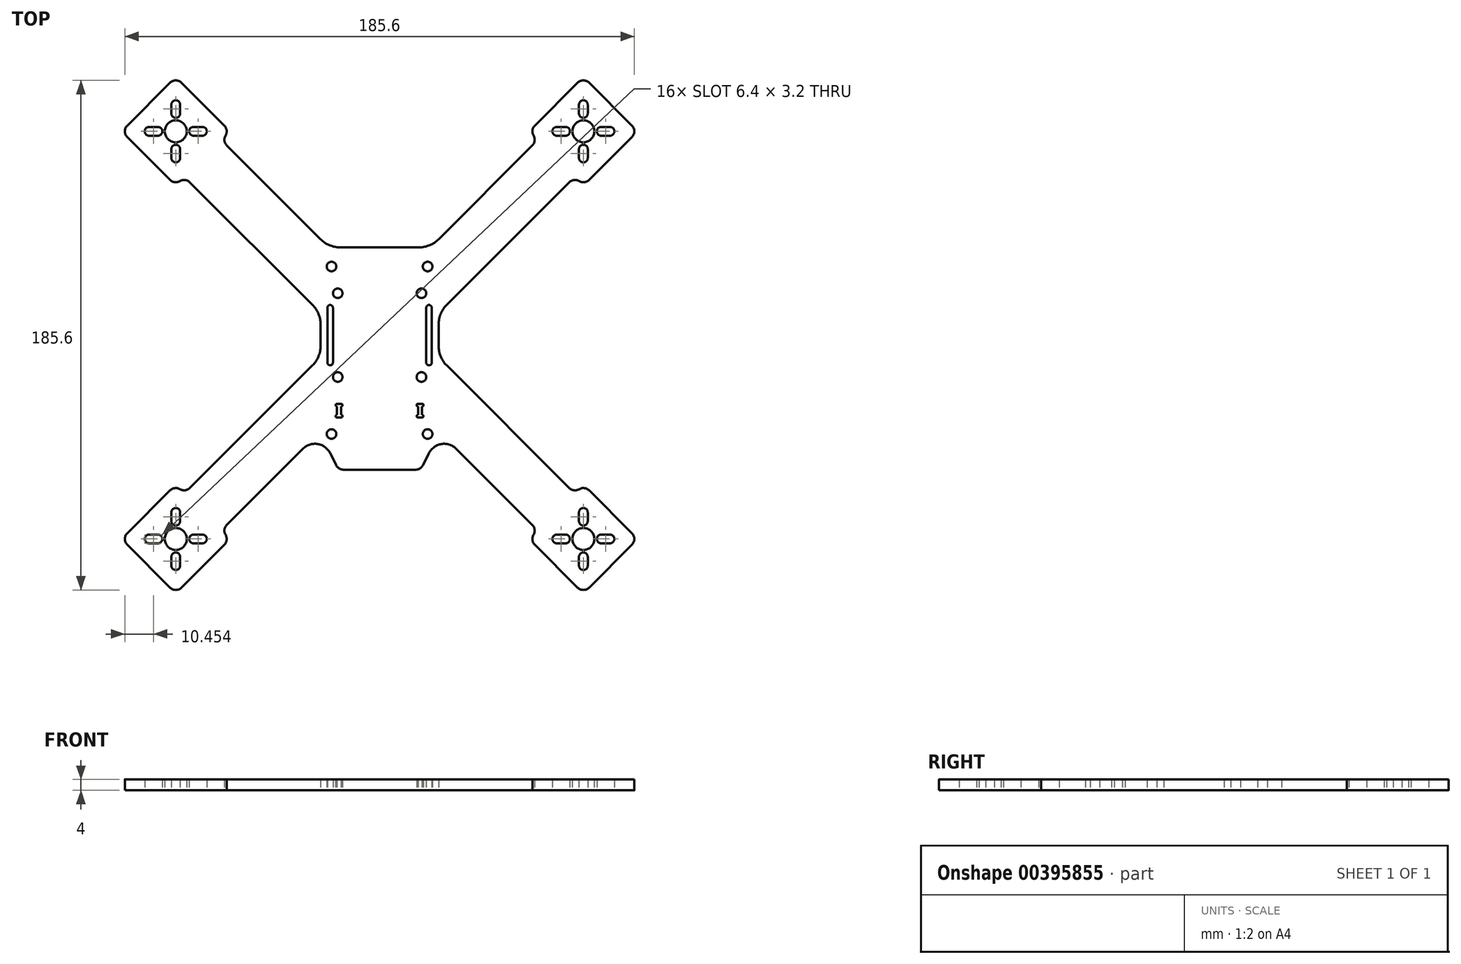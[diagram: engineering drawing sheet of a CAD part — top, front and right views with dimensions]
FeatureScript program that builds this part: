
annotation { "Feature Type Name" : "Feature", "Feature Type Description" : "" }
export const myFeature = defineFeature(function(context is Context, id is Id, definition is map)
    precondition{}
    {
        {
            var Q0;
            Q0=qCreatedBy(makeId("Top.planeOp"),FACE);
            var sketch = newSketch(context, id + "F0", { "sketchPlane" : qUnion([Q0])});
            skLineSegment(sketch, "E0.left", {"start": v(-21.5, 3.92) * mm, "end": v(-21.5, -3.92) * mm});
            skCircle(sketch, "E1", {"center": v(-15.25, 15.25) * mm, "radius": 1.75 * mm});
            skCircle(sketch, "E2", {"center": v(-15.25, -15.25) * mm, "radius": 1.75 * mm});
            skCircle(sketch, "E3.MirrorC", {"center": v(15.25, 15.25) * mm, "radius": 1.75 * mm});
            skCircle(sketch, "E4.MirrorC", {"center": v(15.25, -15.25) * mm, "radius": 1.75 * mm});
            skCircle(sketch, "E5", {"center": v(-17.5, -36) * mm, "radius": 1.75 * mm});
            skCircle(sketch, "E6.MirrorC", {"center": v(17.5, -36) * mm, "radius": 1.75 * mm});
            skLineSegment(sketch, "E7", {"start": v(0, 0) * mm, "end": v(74.25, -74.25) * mm, "construction": true});
            skLineSegment(sketch, "E8", {"start": v(0, 0) * mm, "end": v(74.25, 74.25) * mm, "construction": true});
            skLineSegment(sketch, "E9", {"start": v(0, 0) * mm, "end": v(-74.25, 74.25) * mm, "construction": true});
            skLineSegment(sketch, "E10", {"start": v(0, 0) * mm, "end": v(-74.25, -74.25) * mm, "construction": true});
            skCircle(sketch, "E11", {"center": v(0, 0) * mm, "radius": 105 * mm, "construction": true});
            skCircle(sketch, "E12", {"center": v(74.25, -74.25) * mm, "radius": 63.5 * mm, "construction": true});
            skLineSegment(sketch, "E13.trimOffspring", {"start": v(-13.15, -49) * mm, "end": v(13.15, -49) * mm});
            skPoint(sketch, "E14.visualSharp", {"position": v(-15, -49) * mm});
            skPoint(sketch, "E15.visualSharp", {"position": v(15, -49) * mm});
            skLineSegment(sketch, "E16.bottom", {"start": v(-15.5, -25) * mm, "end": v(-14, -25) * mm});
            skLineSegment(sketch, "E16.top", {"start": v(-15.5, -30) * mm, "end": v(-14, -30) * mm});
            skLineSegment(sketch, "E16.left", {"start": v(-15.5, -26) * mm, "end": v(-15.5, -29) * mm});
            skLineSegment(sketch, "E16.right", {"start": v(-14, -26) * mm, "end": v(-14, -29) * mm});
            skArc(sketch, "E17", {"start": v(-15.5, -25) * mm, "mid": v(-16, -25.5) * mm, "end": v(-15.5, -26) * mm});
            skArc(sketch, "E18", {"start": v(-14, -30) * mm, "mid": v(-13.5, -29.5) * mm, "end": v(-14, -29) * mm});
            skArc(sketch, "E19", {"start": v(-14, -26) * mm, "mid": v(-13.5, -25.5) * mm, "end": v(-14, -25) * mm});
            skArc(sketch, "E20", {"start": v(-15.5, -29) * mm, "mid": v(-16, -29.5) * mm, "end": v(-15.5, -30) * mm});
            skArc(sketch, "E21.MirrorCS", {"start": v(15.5, -25) * mm, "mid": v(16, -25.5) * mm, "end": v(15.5, -26) * mm});
            skArc(sketch, "E22.MirrorCS", {"start": v(15.5, -29) * mm, "mid": v(16, -29.5) * mm, "end": v(15.5, -30) * mm});
            skArc(sketch, "E23.MirrorCS", {"start": v(14, -30) * mm, "mid": v(13.5, -29.5) * mm, "end": v(14, -29) * mm});
            skLineSegment(sketch, "E24.MirrorCS", {"start": v(15.5, -30) * mm, "end": v(14, -30) * mm});
            skLineSegment(sketch, "E25.MirrorCS", {"start": v(15.5, -25) * mm, "end": v(14, -25) * mm});
            skLineSegment(sketch, "E26.MirrorCS", {"start": v(14, -26) * mm, "end": v(14, -29) * mm});
            skLineSegment(sketch, "E27.MirrorCS", {"start": v(15.5, -26) * mm, "end": v(15.5, -29) * mm});
            skArc(sketch, "E28.MirrorCS", {"start": v(14, -26) * mm, "mid": v(13.5, -25.5) * mm, "end": v(14, -25) * mm});
            skLineSegment(sketch, "E29", {"start": v(24.43, 11) * mm, "end": v(71.06, 57.63) * mm});
            skLineSegment(sketch, "E30", {"start": v(21.5, 34.93) * mm, "end": v(57.63, 71.06) * mm});
            skLineSegment(sketch, "E31.trimOffspring", {"start": v(21.5, 3.92) * mm, "end": v(21.5, -3.92) * mm});
            skPoint(sketch, "E32.visualSharp", {"position": v(21.5, 8.06) * mm});
            skArc(sketch, "E32.filletArc", {"start": v(24.43, 11) * mm, "mid": v(22.26, 7.75) * mm, "end": v(21.5, 3.92) * mm});
            skLineSegment(sketch, "E33", {"start": v(24.43, -11) * mm, "end": v(71.06, -57.63) * mm});
            skLineSegment(sketch, "E34", {"start": v(27.95, -41.39) * mm, "end": v(57.63, -71.06) * mm});
            skLineSegment(sketch, "E35", {"start": v(18, -43) * mm, "end": v(15.83, -47.34) * mm});
            skArc(sketch, "E36", {"start": v(27.95, -41.39) * mm, "mid": v(22.56, -39.65) * mm, "end": v(18, -43) * mm});
            skPoint(sketch, "E37.visualSharp", {"position": v(21.5, -8.06) * mm});
            skArc(sketch, "E37.filletArc", {"start": v(21.5, -3.92) * mm, "mid": v(22.26, -7.75) * mm, "end": v(24.43, -11) * mm});
            skLineSegment(sketch, "E38.bottom", {"start": v(72.12, -91.92) * mm, "end": v(56.57, -76.37) * mm});
            skLineSegment(sketch, "E38.top", {"start": v(91.92, -72.12) * mm, "end": v(76.37, -56.57) * mm});
            skLineSegment(sketch, "E38.left", {"start": v(76.37, -91.92) * mm, "end": v(91.92, -76.37) * mm});
            skLineSegment(sketch, "E38.right", {"start": v(56.57, -72.12) * mm, "end": v(57.63, -71.06) * mm});
            skLineSegment(sketch, "E39.trimOffspring", {"start": v(71.06, -57.63) * mm, "end": v(72.12, -56.57) * mm});
            skCircle(sketch, "E40", {"center": v(74.25, -74.25) * mm, "radius": 4 * mm});
            skPoint(sketch, "E41.visualSharp", {"position": v(54.45, -74.25) * mm});
            skArc(sketch, "E41.filletArc", {"start": v(56.57, -72.12) * mm, "mid": v(55.69, -74.25) * mm, "end": v(56.57, -76.37) * mm});
            skPoint(sketch, "E42.visualSharp", {"position": v(74.25, -94.05) * mm});
            skArc(sketch, "E42.filletArc", {"start": v(72.12, -91.92) * mm, "mid": v(74.25, -92.8) * mm, "end": v(76.37, -91.92) * mm});
            skPoint(sketch, "E43.visualSharp", {"position": v(94.05, -74.25) * mm});
            skArc(sketch, "E43.filletArc", {"start": v(91.92, -76.37) * mm, "mid": v(92.8, -74.25) * mm, "end": v(91.92, -72.12) * mm});
            skPoint(sketch, "E44.visualSharp", {"position": v(74.25, -54.45) * mm});
            skArc(sketch, "E44.filletArc", {"start": v(76.37, -56.57) * mm, "mid": v(74.25, -55.69) * mm, "end": v(72.12, -56.57) * mm});
            skLineSegment(sketch, "E45", {"start": v(74.25, -74.25) * mm, "end": v(74.25, -67.75) * mm, "construction": true});
            skLineSegment(sketch, "E46", {"start": v(74.25, -67.75) * mm, "end": v(74.25, -64.55) * mm, "construction": true});
            skLineSegment(sketch, "E47.1.0", {"start": v(74.25, -74.25) * mm, "end": v(67.75, -74.25) * mm, "construction": true});
            skLineSegment(sketch, "E47.1.1", {"start": v(67.75, -74.25) * mm, "end": v(64.55, -74.25) * mm, "construction": true});
            skLineSegment(sketch, "E47.2.0", {"start": v(74.25, -74.25) * mm, "end": v(74.25, -80.75) * mm, "construction": true});
            skLineSegment(sketch, "E47.2.1", {"start": v(74.25, -80.75) * mm, "end": v(74.25, -83.95) * mm, "construction": true});
            skLineSegment(sketch, "E47.3.0", {"start": v(74.25, -74.25) * mm, "end": v(80.75, -74.25) * mm, "construction": true});
            skLineSegment(sketch, "E47.3.1", {"start": v(80.75, -74.25) * mm, "end": v(83.95, -74.25) * mm, "construction": true});
            skArc(sketch, "E48.0.startCap", {"start": v(75.85, -67.75) * mm, "mid": v(74.25, -69.35) * mm, "end": v(72.65, -67.75) * mm});
            skArc(sketch, "E48.0.endCap", {"start": v(72.65, -64.55) * mm, "mid": v(74.25, -62.95) * mm, "end": v(75.85, -64.55) * mm});
            skLineSegment(sketch, "E48.0.left", {"start": v(72.65, -67.75) * mm, "end": v(72.65, -64.55) * mm});
            skLineSegment(sketch, "E48.0.right", {"start": v(75.85, -67.75) * mm, "end": v(75.85, -64.55) * mm});
            skArc(sketch, "E49.0.startCap", {"start": v(80.75, -75.85) * mm, "mid": v(79.15, -74.25) * mm, "end": v(80.75, -72.65) * mm});
            skArc(sketch, "E49.0.endCap", {"start": v(83.95, -72.65) * mm, "mid": v(85.55, -74.25) * mm, "end": v(83.95, -75.85) * mm});
            skLineSegment(sketch, "E49.0.left", {"start": v(80.75, -72.65) * mm, "end": v(83.95, -72.65) * mm});
            skLineSegment(sketch, "E49.0.right", {"start": v(80.75, -75.85) * mm, "end": v(83.95, -75.85) * mm});
            skArc(sketch, "E49.1.startCap", {"start": v(72.65, -80.75) * mm, "mid": v(74.25, -79.15) * mm, "end": v(75.85, -80.75) * mm});
            skArc(sketch, "E49.1.endCap", {"start": v(75.85, -83.95) * mm, "mid": v(74.25, -85.55) * mm, "end": v(72.65, -83.95) * mm});
            skLineSegment(sketch, "E49.1.left", {"start": v(75.85, -80.75) * mm, "end": v(75.85, -83.95) * mm});
            skLineSegment(sketch, "E49.1.right", {"start": v(72.65, -80.75) * mm, "end": v(72.65, -83.95) * mm});
            skArc(sketch, "E49.2.startCap", {"start": v(67.75, -72.65) * mm, "mid": v(69.35, -74.25) * mm, "end": v(67.75, -75.85) * mm});
            skArc(sketch, "E49.2.endCap", {"start": v(64.55, -75.85) * mm, "mid": v(62.95, -74.25) * mm, "end": v(64.55, -72.65) * mm});
            skLineSegment(sketch, "E49.2.left", {"start": v(67.75, -75.85) * mm, "end": v(64.55, -75.85) * mm});
            skLineSegment(sketch, "E49.2.right", {"start": v(67.75, -72.65) * mm, "end": v(64.55, -72.65) * mm});
            skPoint(sketch, "E50.visualSharp", {"position": v(71.06, -57.63) * mm});
            skPoint(sketch, "E51.visualSharp", {"position": v(57.63, -71.06) * mm});
            skLineSegment(sketch, "E52.bottom", {"start": v(19, 10) * mm, "end": v(17, 10) * mm, "construction": true});
            skLineSegment(sketch, "E52.top", {"start": v(19, -10) * mm, "end": v(17, -10) * mm, "construction": true});
            skLineSegment(sketch, "E52.left", {"start": v(19, 10) * mm, "end": v(19, -10) * mm});
            skLineSegment(sketch, "E52.right", {"start": v(17, 10) * mm, "end": v(17, -10) * mm});
            skPoint(sketch, "E52.middle", {"position": v(18, 0) * mm});
            skArc(sketch, "E53", {"start": v(19, 10) * mm, "mid": v(18, 11) * mm, "end": v(17, 10) * mm});
            skArc(sketch, "E54", {"start": v(17, -10) * mm, "mid": v(18, -11) * mm, "end": v(19, -10) * mm});
            skLineSegment(sketch, "E55.MirrorCS", {"start": v(72.65, 67.75) * mm, "end": v(72.65, 64.55) * mm});
            skLineSegment(sketch, "E56.MirrorCS", {"start": v(75.85, 67.75) * mm, "end": v(75.85, 64.55) * mm});
            skArc(sketch, "E57.MirrorCS", {"start": v(75.85, 67.75) * mm, "mid": v(74.25, 69.35) * mm, "end": v(72.65, 67.75) * mm});
            skLineSegment(sketch, "E58.MirrorCS", {"start": v(74.25, 74.25) * mm, "end": v(74.25, 67.75) * mm, "construction": true});
            skLineSegment(sketch, "E59.MirrorCS", {"start": v(74.25, 67.75) * mm, "end": v(74.25, 64.55) * mm, "construction": true});
            skLineSegment(sketch, "E60.MirrorCS", {"start": v(67.75, 74.25) * mm, "end": v(64.55, 74.25) * mm, "construction": true});
            skArc(sketch, "E61.MirrorCS", {"start": v(67.75, 72.65) * mm, "mid": v(69.35, 74.25) * mm, "end": v(67.75, 75.85) * mm});
            skLineSegment(sketch, "E62.MirrorCS", {"start": v(74.25, 74.25) * mm, "end": v(67.75, 74.25) * mm, "construction": true});
            skLineSegment(sketch, "E63.MirrorCS", {"start": v(67.75, 72.65) * mm, "end": v(64.55, 72.65) * mm});
            skLineSegment(sketch, "E64.MirrorCS", {"start": v(67.75, 75.85) * mm, "end": v(64.55, 75.85) * mm});
            skArc(sketch, "E65.MirrorCS", {"start": v(80.75, 75.85) * mm, "mid": v(79.15, 74.25) * mm, "end": v(80.75, 72.65) * mm});
            skLineSegment(sketch, "E66.MirrorCS", {"start": v(72.65, 80.75) * mm, "end": v(72.65, 83.95) * mm});
            skCircle(sketch, "E67.MirrorC", {"center": v(74.25, 74.25) * mm, "radius": 4 * mm});
            skLineSegment(sketch, "E68.MirrorCS", {"start": v(74.25, 74.25) * mm, "end": v(74.25, 80.75) * mm, "construction": true});
            skArc(sketch, "E69.MirrorCS", {"start": v(83.95, 72.65) * mm, "mid": v(85.55, 74.25) * mm, "end": v(83.95, 75.85) * mm});
            skLineSegment(sketch, "E70.MirrorCS", {"start": v(75.85, 80.75) * mm, "end": v(75.85, 83.95) * mm});
            skLineSegment(sketch, "E71.MirrorCS", {"start": v(74.25, 80.75) * mm, "end": v(74.25, 83.95) * mm, "construction": true});
            skLineSegment(sketch, "E72.MirrorCS", {"start": v(71.06, 57.63) * mm, "end": v(72.12, 56.57) * mm});
            skLineSegment(sketch, "E73.MirrorCS", {"start": v(56.57, 72.12) * mm, "end": v(57.63, 71.06) * mm});
            skArc(sketch, "E74.MirrorCS", {"start": v(72.65, 64.55) * mm, "mid": v(74.25, 62.95) * mm, "end": v(75.85, 64.55) * mm});
            skArc(sketch, "E75.MirrorCS", {"start": v(75.85, 83.95) * mm, "mid": v(74.25, 85.55) * mm, "end": v(72.65, 83.95) * mm});
            skLineSegment(sketch, "E76.MirrorCS", {"start": v(80.75, 74.25) * mm, "end": v(83.95, 74.25) * mm, "construction": true});
            skLineSegment(sketch, "E77.MirrorCS", {"start": v(80.75, 75.85) * mm, "end": v(83.95, 75.85) * mm});
            skArc(sketch, "E78.MirrorCS", {"start": v(72.65, 80.75) * mm, "mid": v(74.25, 79.15) * mm, "end": v(75.85, 80.75) * mm});
            skLineSegment(sketch, "E79.MirrorCS", {"start": v(80.75, 72.65) * mm, "end": v(83.95, 72.65) * mm});
            skLineSegment(sketch, "E80.MirrorCS", {"start": v(74.25, 74.25) * mm, "end": v(80.75, 74.25) * mm, "construction": true});
            skArc(sketch, "E81.MirrorCS", {"start": v(56.57, 72.12) * mm, "mid": v(55.69, 74.25) * mm, "end": v(56.57, 76.37) * mm});
            skArc(sketch, "E82.MirrorCS", {"start": v(72.12, 91.92) * mm, "mid": v(74.25, 92.8) * mm, "end": v(76.37, 91.92) * mm});
            skArc(sketch, "E83.MirrorCS", {"start": v(64.55, 75.85) * mm, "mid": v(62.95, 74.25) * mm, "end": v(64.55, 72.65) * mm});
            skArc(sketch, "E84.MirrorCS", {"start": v(76.37, 56.57) * mm, "mid": v(74.25, 55.69) * mm, "end": v(72.12, 56.57) * mm});
            skArc(sketch, "E85.MirrorCS", {"start": v(91.92, 76.37) * mm, "mid": v(92.8, 74.25) * mm, "end": v(91.92, 72.12) * mm});
            skPoint(sketch, "E86.MirrorP", {"position": v(71.06, 57.63) * mm});
            skPoint(sketch, "E87.MirrorP", {"position": v(74.25, 94.05) * mm});
            skPoint(sketch, "E88.MirrorP", {"position": v(54.45, 74.25) * mm});
            skPoint(sketch, "E89.MirrorP", {"position": v(57.63, 71.06) * mm});
            skLineSegment(sketch, "E90.MirrorCS", {"start": v(76.37, 91.92) * mm, "end": v(91.92, 76.37) * mm});
            skLineSegment(sketch, "E91.MirrorCS", {"start": v(91.92, 72.12) * mm, "end": v(76.37, 56.57) * mm});
            skPoint(sketch, "E92.MirrorP", {"position": v(74.25, 54.45) * mm});
            skPoint(sketch, "E93.MirrorP", {"position": v(94.05, 74.25) * mm});
            skLineSegment(sketch, "E94.MirrorCS", {"start": v(72.12, 91.92) * mm, "end": v(56.57, 76.37) * mm});
            skLineSegment(sketch, "E95.MirrorCS", {"start": v(-56.57, -72.12) * mm, "end": v(-57.63, -71.06) * mm});
            skLineSegment(sketch, "E96.MirrorCS", {"start": v(-74.25, 74.25) * mm, "end": v(-74.25, 80.75) * mm, "construction": true});
            skLineSegment(sketch, "E97.MirrorCS", {"start": v(-74.25, 74.25) * mm, "end": v(-80.75, 74.25) * mm, "construction": true});
            skLineSegment(sketch, "E98.MirrorCS", {"start": v(-74.25, -74.25) * mm, "end": v(-74.25, -67.75) * mm, "construction": true});
            skLineSegment(sketch, "E99.MirrorCS", {"start": v(-80.75, 75.85) * mm, "end": v(-83.95, 75.85) * mm});
            skArc(sketch, "E100.MirrorCS", {"start": v(-80.75, -75.85) * mm, "mid": v(-79.15, -74.25) * mm, "end": v(-80.75, -72.65) * mm});
            skLineSegment(sketch, "E101.MirrorCS", {"start": v(-80.75, 74.25) * mm, "end": v(-83.95, 74.25) * mm, "construction": true});
            skLineSegment(sketch, "E102.MirrorCS", {"start": v(-75.85, -67.75) * mm, "end": v(-75.85, -64.55) * mm});
            skLineSegment(sketch, "E103.MirrorCS", {"start": v(-72.65, -67.75) * mm, "end": v(-72.65, -64.55) * mm});
            skLineSegment(sketch, "E104.MirrorCS", {"start": v(-74.25, 74.25) * mm, "end": v(-74.25, 67.75) * mm, "construction": true});
            skArc(sketch, "E105.MirrorCS", {"start": v(-72.65, 80.75) * mm, "mid": v(-74.25, 79.15) * mm, "end": v(-75.85, 80.75) * mm});
            skLineSegment(sketch, "E106.MirrorCS", {"start": v(-74.25, 74.25) * mm, "end": v(-67.75, 74.25) * mm, "construction": true});
            skArc(sketch, "E107.MirrorCS", {"start": v(-67.75, -72.65) * mm, "mid": v(-69.35, -74.25) * mm, "end": v(-67.75, -75.85) * mm});
            skLineSegment(sketch, "E108.MirrorCS", {"start": v(-75.85, 80.75) * mm, "end": v(-75.85, 83.95) * mm});
            skLineSegment(sketch, "E109.MirrorCS", {"start": v(-56.57, 72.12) * mm, "end": v(-57.63, 71.06) * mm});
            skLineSegment(sketch, "E110.MirrorCS", {"start": v(-67.75, -72.65) * mm, "end": v(-64.55, -72.65) * mm});
            skLineSegment(sketch, "E111.MirrorCS", {"start": v(-80.75, -74.25) * mm, "end": v(-83.95, -74.25) * mm, "construction": true});
            skLineSegment(sketch, "E112.MirrorCS", {"start": v(-80.75, -72.65) * mm, "end": v(-83.95, -72.65) * mm});
            skLineSegment(sketch, "E113.MirrorCS", {"start": v(-74.25, -67.75) * mm, "end": v(-74.25, -64.55) * mm, "construction": true});
            skLineSegment(sketch, "E114.MirrorCS", {"start": v(-72.65, 80.75) * mm, "end": v(-72.65, 83.95) * mm});
            skLineSegment(sketch, "E115.MirrorCS", {"start": v(-67.75, -74.25) * mm, "end": v(-64.55, -74.25) * mm, "construction": true});
            skArc(sketch, "E116.MirrorCS", {"start": v(-80.75, 75.85) * mm, "mid": v(-79.15, 74.25) * mm, "end": v(-80.75, 72.65) * mm});
            skLineSegment(sketch, "E117.MirrorCS", {"start": v(-74.25, -74.25) * mm, "end": v(-67.75, -74.25) * mm, "construction": true});
            skLineSegment(sketch, "E118.MirrorCS", {"start": v(-80.75, 72.65) * mm, "end": v(-83.95, 72.65) * mm});
            skLineSegment(sketch, "E119.MirrorCS", {"start": v(-67.75, -75.85) * mm, "end": v(-64.55, -75.85) * mm});
            skLineSegment(sketch, "E120.MirrorCS", {"start": v(-80.75, -75.85) * mm, "end": v(-83.95, -75.85) * mm});
            skLineSegment(sketch, "E121.MirrorCS", {"start": v(-74.25, 80.75) * mm, "end": v(-74.25, 83.95) * mm, "construction": true});
            skLineSegment(sketch, "E122.MirrorCS", {"start": v(-74.25, -74.25) * mm, "end": v(-80.75, -74.25) * mm, "construction": true});
            skArc(sketch, "E123.MirrorCS", {"start": v(-75.85, -67.75) * mm, "mid": v(-74.25, -69.35) * mm, "end": v(-72.65, -67.75) * mm});
            skArc(sketch, "E124.MirrorCS", {"start": v(-67.75, 72.65) * mm, "mid": v(-69.35, 74.25) * mm, "end": v(-67.75, 75.85) * mm});
            skLineSegment(sketch, "E125.MirrorCS", {"start": v(-67.75, 74.25) * mm, "end": v(-64.55, 74.25) * mm, "construction": true});
            skCircle(sketch, "E126.MirrorC", {"center": v(-74.25, -74.25) * mm, "radius": 4 * mm});
            skLineSegment(sketch, "E127.MirrorCS", {"start": v(-71.06, -57.63) * mm, "end": v(-72.12, -56.57) * mm});
            skLineSegment(sketch, "E128.MirrorCS", {"start": v(-74.25, 67.75) * mm, "end": v(-74.25, 64.55) * mm, "construction": true});
            skArc(sketch, "E129.MirrorCS", {"start": v(-72.65, -64.55) * mm, "mid": v(-74.25, -62.95) * mm, "end": v(-75.85, -64.55) * mm});
            skArc(sketch, "E130.MirrorCS", {"start": v(-83.95, -72.65) * mm, "mid": v(-85.55, -74.25) * mm, "end": v(-83.95, -75.85) * mm});
            skArc(sketch, "E131.MirrorCS", {"start": v(-72.12, -91.92) * mm, "mid": v(-74.25, -92.8) * mm, "end": v(-76.37, -91.92) * mm});
            skLineSegment(sketch, "E132.MirrorCS", {"start": v(-74.25, -74.25) * mm, "end": v(-74.25, -80.75) * mm, "construction": true});
            skLineSegment(sketch, "E133.MirrorCS", {"start": v(-74.25, -80.75) * mm, "end": v(-74.25, -83.95) * mm, "construction": true});
            skArc(sketch, "E134.MirrorCS", {"start": v(-64.55, -75.85) * mm, "mid": v(-62.95, -74.25) * mm, "end": v(-64.55, -72.65) * mm});
            skArc(sketch, "E135.MirrorCS", {"start": v(-75.85, 67.75) * mm, "mid": v(-74.25, 69.35) * mm, "end": v(-72.65, 67.75) * mm});
            skLineSegment(sketch, "E136.MirrorCS", {"start": v(-72.65, -80.75) * mm, "end": v(-72.65, -83.95) * mm});
            skArc(sketch, "E137.MirrorCS", {"start": v(-75.85, -83.95) * mm, "mid": v(-74.25, -85.55) * mm, "end": v(-72.65, -83.95) * mm});
            skLineSegment(sketch, "E138.MirrorCS", {"start": v(-71.06, 57.63) * mm, "end": v(-72.12, 56.57) * mm});
            skLineSegment(sketch, "E139.MirrorCS", {"start": v(-67.75, 72.65) * mm, "end": v(-64.55, 72.65) * mm});
            skLineSegment(sketch, "E140.MirrorCS", {"start": v(-67.75, 75.85) * mm, "end": v(-64.55, 75.85) * mm});
            skArc(sketch, "E141.MirrorCS", {"start": v(-72.65, -80.75) * mm, "mid": v(-74.25, -79.15) * mm, "end": v(-75.85, -80.75) * mm});
            skArc(sketch, "E142.MirrorCS", {"start": v(-76.37, -56.57) * mm, "mid": v(-74.25, -55.69) * mm, "end": v(-72.12, -56.57) * mm});
            skCircle(sketch, "E143.MirrorC", {"center": v(-74.25, 74.25) * mm, "radius": 4 * mm});
            skLineSegment(sketch, "E144.MirrorCS", {"start": v(-72.65, 67.75) * mm, "end": v(-72.65, 64.55) * mm});
            skLineSegment(sketch, "E145.MirrorCS", {"start": v(-75.85, -80.75) * mm, "end": v(-75.85, -83.95) * mm});
            skLineSegment(sketch, "E146.MirrorCS", {"start": v(-75.85, 67.75) * mm, "end": v(-75.85, 64.55) * mm});
            skArc(sketch, "E147.MirrorCS", {"start": v(-56.57, -72.12) * mm, "mid": v(-55.69, -74.25) * mm, "end": v(-56.57, -76.37) * mm});
            skArc(sketch, "E148.MirrorCS", {"start": v(-75.85, 83.95) * mm, "mid": v(-74.25, 85.55) * mm, "end": v(-72.65, 83.95) * mm});
            skArc(sketch, "E149.MirrorCS", {"start": v(-72.65, 64.55) * mm, "mid": v(-74.25, 62.95) * mm, "end": v(-75.85, 64.55) * mm});
            skArc(sketch, "E150.MirrorCS", {"start": v(-83.95, 72.65) * mm, "mid": v(-85.55, 74.25) * mm, "end": v(-83.95, 75.85) * mm});
            skArc(sketch, "E151.MirrorCS", {"start": v(-76.37, 56.57) * mm, "mid": v(-74.25, 55.69) * mm, "end": v(-72.12, 56.57) * mm});
            skArc(sketch, "E152.MirrorCS", {"start": v(-64.55, 75.85) * mm, "mid": v(-62.95, 74.25) * mm, "end": v(-64.55, 72.65) * mm});
            skArc(sketch, "E153.MirrorCS", {"start": v(-91.92, -76.37) * mm, "mid": v(-92.8, -74.25) * mm, "end": v(-91.92, -72.12) * mm});
            skArc(sketch, "E154.MirrorCS", {"start": v(-56.57, 72.12) * mm, "mid": v(-55.69, 74.25) * mm, "end": v(-56.57, 76.37) * mm});
            skArc(sketch, "E155.MirrorCS", {"start": v(-91.92, 76.37) * mm, "mid": v(-92.8, 74.25) * mm, "end": v(-91.92, 72.12) * mm});
            skArc(sketch, "E156.MirrorCS", {"start": v(-72.12, 91.92) * mm, "mid": v(-74.25, 92.8) * mm, "end": v(-76.37, 91.92) * mm});
            skLineSegment(sketch, "E157.MirrorCS", {"start": v(-72.12, 91.92) * mm, "end": v(-56.57, 76.37) * mm});
            skPoint(sketch, "E158.MirrorP", {"position": v(-57.63, -71.06) * mm});
            skPoint(sketch, "E159.MirrorP", {"position": v(-71.06, 57.63) * mm});
            skPoint(sketch, "E160.MirrorP", {"position": v(-74.25, -54.45) * mm});
            skLineSegment(sketch, "E161.MirrorCS", {"start": v(-91.92, 72.12) * mm, "end": v(-76.37, 56.57) * mm});
            skPoint(sketch, "E162.MirrorP", {"position": v(-94.05, -74.25) * mm});
            skPoint(sketch, "E163.MirrorP", {"position": v(-74.25, 94.05) * mm});
            skLineSegment(sketch, "E164.MirrorCS", {"start": v(-91.92, -72.12) * mm, "end": v(-76.37, -56.57) * mm});
            skPoint(sketch, "E165.MirrorP", {"position": v(-74.25, -94.05) * mm});
            skPoint(sketch, "E166.MirrorP", {"position": v(-74.25, 54.45) * mm});
            skPoint(sketch, "E167.MirrorP", {"position": v(-54.45, -74.25) * mm});
            skPoint(sketch, "E168.MirrorP", {"position": v(-94.05, 74.25) * mm});
            skPoint(sketch, "E169.MirrorP", {"position": v(-54.45, 74.25) * mm});
            skPoint(sketch, "E170.MirrorP", {"position": v(-57.63, 71.06) * mm});
            skLineSegment(sketch, "E171.MirrorCS", {"start": v(-76.37, 91.92) * mm, "end": v(-91.92, 76.37) * mm});
            skLineSegment(sketch, "E172.MirrorCS", {"start": v(-72.12, -91.92) * mm, "end": v(-56.57, -76.37) * mm});
            skLineSegment(sketch, "E173.MirrorCS", {"start": v(-76.37, -91.92) * mm, "end": v(-91.92, -76.37) * mm});
            skLineSegment(sketch, "E174.MirrorCS", {"start": v(-21.5, 34.93) * mm, "end": v(-57.63, 71.06) * mm});
            skLineSegment(sketch, "E175.MirrorCS", {"start": v(-24.43, 11) * mm, "end": v(-71.06, 57.63) * mm});
            skLineSegment(sketch, "E176.MirrorCS", {"start": v(-24.43, -11) * mm, "end": v(-71.06, -57.63) * mm});
            skLineSegment(sketch, "E177.MirrorCS", {"start": v(-27.95, -41.39) * mm, "end": v(-57.63, -71.06) * mm});
            skArc(sketch, "E178.MirrorCS", {"start": v(-24.43, 11) * mm, "mid": v(-22.26, 7.75) * mm, "end": v(-21.5, 3.92) * mm});
            skArc(sketch, "E179.MirrorCS", {"start": v(-21.5, -3.92) * mm, "mid": v(-22.26, -7.75) * mm, "end": v(-24.43, -11) * mm});
            skLineSegment(sketch, "E180.MirrorCS", {"start": v(-18, -43) * mm, "end": v(-15.83, -47.34) * mm});
            skArc(sketch, "E181.MirrorCS", {"start": v(-27.95, -41.39) * mm, "mid": v(-22.56, -39.65) * mm, "end": v(-18, -43) * mm});
            skArc(sketch, "E182.MirrorCS", {"start": v(-19, 10) * mm, "mid": v(-18, 11) * mm, "end": v(-17, 10) * mm});
            skLineSegment(sketch, "E183.MirrorCS", {"start": v(-19, 10) * mm, "end": v(-17, 10) * mm, "construction": true});
            skLineSegment(sketch, "E184.MirrorCS", {"start": v(-19, 10) * mm, "end": v(-19, -10) * mm});
            skLineSegment(sketch, "E185.MirrorCS", {"start": v(-17, 10) * mm, "end": v(-17, -10) * mm});
            skArc(sketch, "E186.MirrorCS", {"start": v(-17, -10) * mm, "mid": v(-18, -11) * mm, "end": v(-19, -10) * mm});
            skArc(sketch, "E187.filletArc", {"start": v(-15.83, -47.34) * mm, "mid": v(-14.72, -48.55) * mm, "end": v(-13.15, -49) * mm});
            skArc(sketch, "E188.filletArc", {"start": v(13.15, -49) * mm, "mid": v(14.72, -48.55) * mm, "end": v(15.83, -47.34) * mm});
            skCircle(sketch, "E189", {"center": v(-17.5, 25) * mm, "radius": 1.75 * mm});
            skCircle(sketch, "E190.MirrorC", {"center": v(17.5, 25) * mm, "radius": 1.75 * mm});
            skCircle(sketch, "E191.MirrorC", {"center": v(74.25, 74.25) * mm, "radius": 63.5 * mm, "construction": true});
            skLineSegment(sketch, "E192", {"start": v(-14.42, 32) * mm, "end": v(14.42, 32) * mm});
            skPoint(sketch, "E193.visualSharp", {"position": v(-18.56, 32) * mm});
            skArc(sketch, "E193.filletArc", {"start": v(-21.5, 34.93) * mm, "mid": v(-18.25, 32.76) * mm, "end": v(-14.42, 32) * mm});
            skPoint(sketch, "E194.visualSharp", {"position": v(18.56, 32) * mm});
            skArc(sketch, "E194.filletArc", {"start": v(14.42, 32) * mm, "mid": v(18.25, 32.76) * mm, "end": v(21.5, 34.93) * mm});
            skSolve(sketch);
        }
        {
            var Q0;
            Q0 = qSketchRegion(id + "F0", true);
            extrude(context, id + "F1", {"entities" : qUnion([Q0]), "depth" : 4 * mm});
        }
        {
            var Q0;
            Q0=makeQuery(id+"F1.opExtrude","SWEPT_EDGE",EDGE,{"disambiguationData":[OSD([sQuery(id+"F0.wireOp",EDGE,"E138.MirrorCS"),sQuery(id+"F0.wireOp",EDGE,"E175.MirrorCS")])]});
            var Q1;
            Q1=makeQuery(id+"F1.opExtrude","SWEPT_EDGE",EDGE,{"disambiguationData":[OSD([sQuery(id+"F0.wireOp",EDGE,"E109.MirrorCS"),sQuery(id+"F0.wireOp",EDGE,"E174.MirrorCS")])]});
            var Q2;
            Q2=makeQuery(id+"F1.opExtrude","SWEPT_EDGE",EDGE,{"disambiguationData":[OSD([sQuery(id+"F0.wireOp",EDGE,"E95.MirrorCS"),sQuery(id+"F0.wireOp",EDGE,"E177.MirrorCS")])]});
            var Q3;
            Q3=makeQuery(id+"F1.opExtrude","SWEPT_EDGE",EDGE,{"disambiguationData":[OSD([sQuery(id+"F0.wireOp",EDGE,"E127.MirrorCS"),sQuery(id+"F0.wireOp",EDGE,"E176.MirrorCS")])]});
            var Q4;
            Q4=makeQuery(id+"F1.opExtrude","SWEPT_EDGE",EDGE,{"disambiguationData":[OSD([sQuery(id+"F0.wireOp",EDGE,"E29"),sQuery(id+"F0.wireOp",EDGE,"E72.MirrorCS")])]});
            var Q5;
            Q5=makeQuery(id+"F1.opExtrude","SWEPT_EDGE",EDGE,{"disambiguationData":[OSD([sQuery(id+"F0.wireOp",EDGE,"E30"),sQuery(id+"F0.wireOp",EDGE,"E73.MirrorCS")])]});
            var Q6;
            Q6=makeQuery(id+"F1.opExtrude","SWEPT_EDGE",EDGE,{"disambiguationData":[OSD([sQuery(id+"F0.wireOp",EDGE,"E34"),sQuery(id+"F0.wireOp",EDGE,"E38.right")])]});
            var Q7;
            Q7=makeQuery(id+"F1.opExtrude","SWEPT_EDGE",EDGE,{"disambiguationData":[OSD([sQuery(id+"F0.wireOp",EDGE,"E33"),sQuery(id+"F0.wireOp",EDGE,"E39.trimOffspring")])]});
            fillet(context, id + "F2", {"entities" : qUnion([Q0, Q1, Q2, Q3, Q4, Q5, Q6, Q7]), "radius" : 3 * mm, "tangentPropagation" : true, "allowEdgeOverflow" : false});
        }
    });
